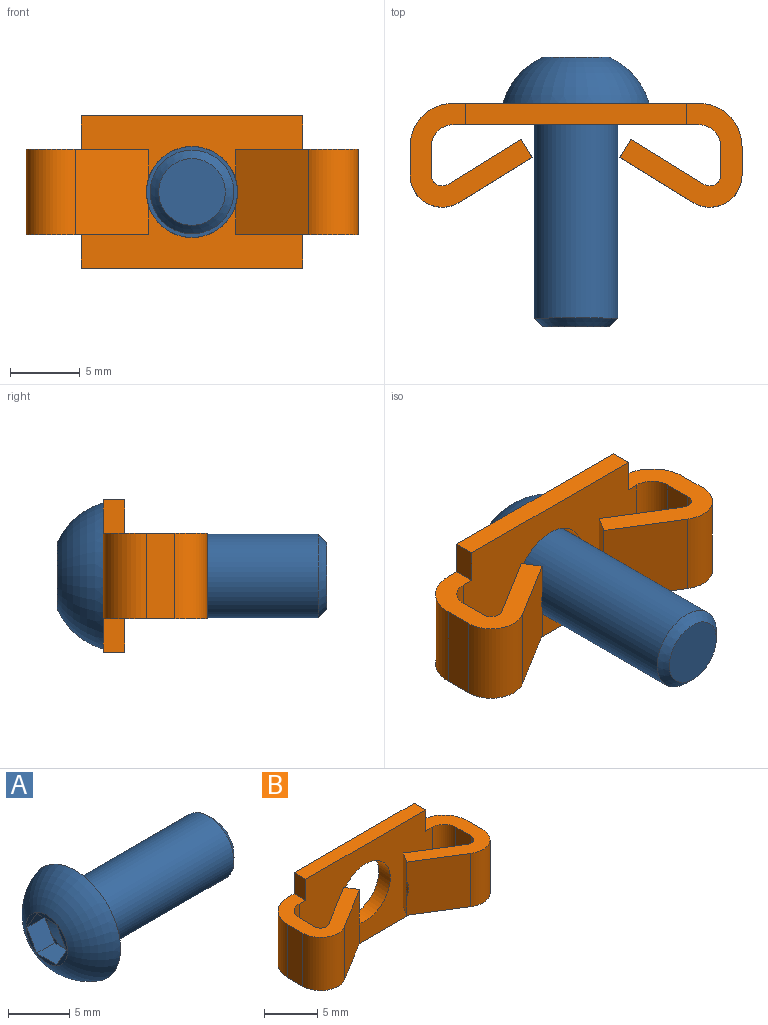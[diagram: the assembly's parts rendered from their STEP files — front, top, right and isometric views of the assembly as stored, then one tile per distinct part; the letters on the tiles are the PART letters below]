
ASSEMBLY  parts=2 mates=1
PART A: 19 faces, bbox 19.3x10.5x10.5 mm
  f0: plane 1.73x1mm, normal (-1,0,0), area 0.2mm2, adj f9,f14,f15
  f1: plane 2x0.58mm, normal (-1,0,0), area 0.2mm2, adj f13,f14,f15
  f2: plane 1.73x1mm, normal (-1,0,0), area 0.2mm2, adj f9,f10,f15
  f3: plane 4.8x4.8mm, normal (-1,0,0), area 4.2mm2, adj f4,f9,f10,f11,f12,f13,f14
  f4: torus R=0.21mm, axis (1,0,0), area 114.8mm2, adj f3,f5
  f5: plane 10.5x10.5mm, normal (1,0,0), area 58.3mm2, adj f4,f6
  f6: cylinder r=3mm len=15.39mm, axis (-1,0,0), area 290mm2, adj f5,f7
  f7: cone r=3mm half-angle=45deg, axis (-1,0,0), area 14.7mm2, adj f6,f8
  f8: plane 4.77x4.77mm, normal (1,0,0), area 17.9mm2, adj f7
  f9: plane 2.31x2.08mm, normal (0,0,-1), area 4.8mm2, adj f0,f2,f3,f10,f14
  f10: plane 2.08x2mm, normal (0,0.87,-0.5), area 4.8mm2, adj f2,f3,f9,f11,f18
  f11: plane 2.08x2mm, normal (0,0.87,0.5), area 4.8mm2, adj f3,f10,f12,f17,f18
  f12: plane 2.31x2.08mm, normal (0,0,1), area 4.8mm2, adj f3,f11,f13,f16,f17
  f13: plane 2.08x2mm, normal (0,-0.87,0.5), area 4.8mm2, adj f1,f3,f12,f14,f16
  f14: plane 2.08x2mm, normal (0,-0.87,-0.5), area 4.8mm2, adj f0,f1,f3,f9,f13
  f15: cone r=866.03mm half-angle=60deg, axis (-1,0,0), area 14.5mm2, adj f0,f1,f2,f16,f17,f18
  f16: plane 1.73x1mm, normal (-1,0,0), area 0.2mm2, adj f12,f13,f15
  f17: plane 1.73x1mm, normal (-1,0,0), area 0.2mm2, adj f11,f12,f15
  f18: plane 2x0.58mm, normal (-1,0,0), area 0.2mm2, adj f10,f11,f15
PART B: 33 faces, bbox 23.8x7.4x10.9 mm
  f0: cylinder r=3.26mm len=6.53mm, axis (0,1,0), area 31.3mm2, adj f8,f18
  f1: cylinder r=3.26mm len=1.8mm, axis (0,1,0), area 0.3mm2, adj f12,f13
  f2: plane 15.88x1.52mm, normal (0,0,1), area 24.2mm2, adj f8,f18,f31,f32
  f3: cylinder r=3.26mm len=1.8mm, axis (0,1,0), area 0.3mm2, adj f23,f24
  f4: plane 8.76x7.44mm, normal (0,0,1), area 24.4mm2, adj f7,f8,f18,f19,f20,f21,f22,f23
  f5: plane 8.76x7.44mm, normal (0,0,1), area 24.4mm2, adj f8,f9,f10,f11,f12,f13,f14,f15
  f6: plane 8.76x7.44mm, normal (0,0,-1), area 24.4mm2, adj f7,f8,f18,f19,f20,f21,f22,f23
  f7: cylinder r=3.1mm len=6.1mm, axis (0,0,1), area 29.7mm2, adj f4,f6,f8,f26
  f8: plane 17.6x10.92mm, normal (0,1,0), area 150.4mm2, adj f0,f2,f4,f5,f6,f7,f9,f27
  f9: cylinder r=3.1mm len=6.1mm, axis (0,0,1), area 29.7mm2, adj f5,f8,f10,f27
  f10: plane 6.1x2.03mm, normal (1,0,0), area 12.4mm2, adj f5,f9,f11,f27
  f11: cylinder r=2.31mm len=6.1mm, axis (0,0,1), area 29.9mm2, adj f5,f10,f12,f27
  f12: plane 6.1x5.23mm, normal (-0.53,-0.85,0), area 37.4mm2, adj f1,f5,f11,f13,f27
  f13: plane 6.1x1.3mm, normal (-0.85,0.53,0), area 9mm2, adj f1,f5,f12,f14,f27
  f14: plane 6.1x5.23mm, normal (0.53,0.85,0), area 37.5mm2, adj f5,f13,f15,f27
  f15: cylinder r=0.79mm len=6.1mm, axis (0,0,1), area 10.2mm2, adj f5,f14,f16,f27
  f16: plane 6.1x2.03mm, normal (-1,0,0), area 12.4mm2, adj f5,f15,f17,f27
  f17: cylinder r=1.57mm len=6.1mm, axis (0,0,1), area 15.1mm2, adj f5,f16,f18,f27
  f18: plane 17.6x10.92mm, normal (0,-1,0), area 150.4mm2, adj f0,f2,f4,f5,f6,f17,f19,f27
  f19: cylinder r=1.57mm len=6.1mm, axis (0,0,1), area 15.1mm2, adj f4,f6,f18,f20
  f20: plane 6.1x2.03mm, normal (1,0,0), area 12.4mm2, adj f4,f6,f19,f21
  f21: cylinder r=0.79mm len=6.1mm, axis (0,0,1), area 10.2mm2, adj f4,f6,f20,f22
  f22: plane 6.1x5.23mm, normal (-0.53,0.85,0), area 37.5mm2, adj f4,f6,f21,f23
  f23: plane 6.1x1.3mm, normal (0.85,0.53,0), area 9mm2, adj f3,f4,f6,f22,f24
  f24: plane 6.1x5.23mm, normal (0.53,-0.85,0), area 37.4mm2, adj f3,f4,f6,f23,f25
  f25: cylinder r=2.31mm len=6.1mm, axis (0,0,1), area 29.9mm2, adj f4,f6,f24,f26
  f26: plane 6.1x2.03mm, normal (-1,0,0), area 12.4mm2, adj f4,f6,f7,f25
  f27: plane 8.76x7.44mm, normal (0,0,-1), area 24.4mm2, adj f8,f9,f10,f11,f12,f13,f14,f15
  f28: plane 15.88x1.52mm, normal (0,0,-1), area 24.2mm2, adj f8,f18,f29,f30
  f29: plane 2.41x1.52mm, normal (1,0,0), area 3.7mm2, adj f8,f18,f27,f28
  f30: plane 2.41x1.52mm, normal (-1,0,0), area 3.7mm2, adj f6,f8,f18,f28
  f31: plane 2.41x1.52mm, normal (-1,0,0), area 3.7mm2, adj f2,f4,f8,f18
  f32: plane 2.41x1.52mm, normal (1,0,0), area 3.7mm2, adj f2,f5,f8,f18
PLACE A rot(axis=(0.58,-0.58,-0.58),120deg) t=(0,7.44,0)mm
PLACE B at identity
MATE fastened A.f15 <-> B.f0  axis (0,-1,0) through (0,7.44,0)mm
